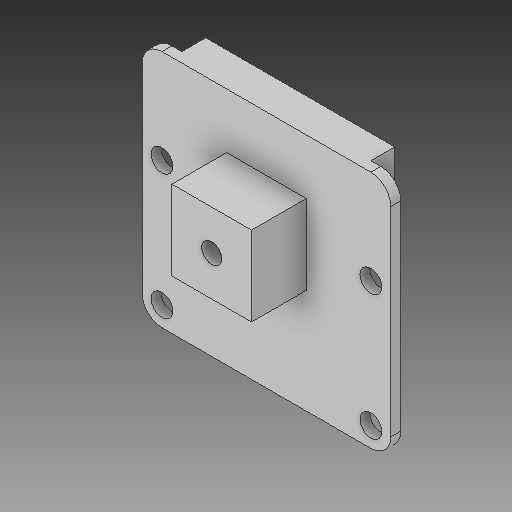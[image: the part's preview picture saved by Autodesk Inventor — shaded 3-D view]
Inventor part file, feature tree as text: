
AUTODESK INVENTOR PART (.ipt)
format: ipt  version: 2019.3 (Build 233278000, 278)  size: 158,720 bytes
history: native  units: in
note: dims shown in document units (in); Inventor stores cm internally (conversion verified against a paired STEP export)
features: extrude x4, sketch x4, fillet x1
ambient origin geometry x8: Origin, YZ Plane, XZ Plane, XY Plane, X Axis, Y Axis, Z Axis, Center Point
bodies: Solid1 (feature_tree)
feature tree (9):
  extrude  "Extrusion1"  Depth=0.0787in
  extrude  "Extrusion2"  Depth=0.0787in
  extrude  "Extrusion3"  Depth=0.9843in
  fillet  "Fillet1"  Radius=0.0866in
  extrude  "Extrusion4"  Depth=0.0945in
  sketch  "Sketch1"  dims[d0=0.0787in d1=0.0787in]
  sketch  "Sketch2"  dims[d2=0.0787in d3=0.4953in]
  sketch  "Sketch5"  dims[d4=0.3725in d5=0.9843in d6=0.0866in]
  sketch  "Sketch6"  dims[d7=0.0394in d8=0.0in d9=0.5709in d10=0.315in d11=0.2165in d12=0.0in d13=0.0787in d14=5.5in d15=0.0in d16=0.0787in d17=0.1969in d18=0.748in d19=0.0945in d20=0.0in]
